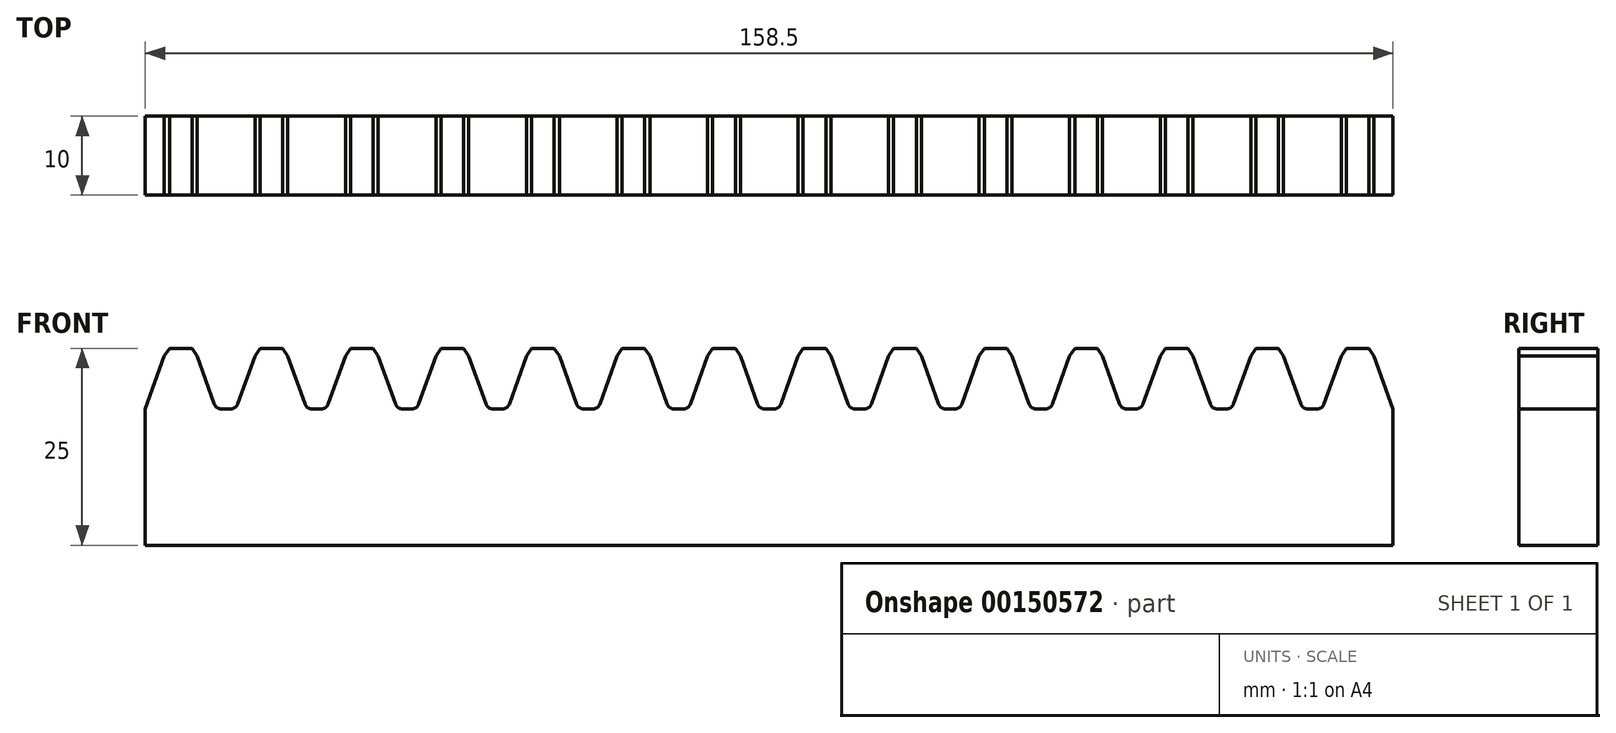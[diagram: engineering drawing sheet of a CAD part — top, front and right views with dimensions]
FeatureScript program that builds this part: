
annotation { "Feature Type Name" : "Feature", "Feature Type Description" : "" }
export const myFeature = defineFeature(function(context is Context, id is Id, definition is map)
    precondition{}
    {
        {
            var Q0;
            Q0=qCreatedBy(makeId("Front.planeOp"),FACE);
            var sketch = newSketch(context, id + "F0", { "sketchPlane" : qUnion([Q0])});
            skLineSegment(sketch, "E0", {"start": v(0, 0) * mm, "end": v(151.35, 0) * mm, "construction": true});
            skLineSegment(sketch, "E1.bottom", {"start": v(0, 0) * mm, "end": v(9, 0) * mm});
            skLineSegment(sketch, "E1.top", {"start": v(2.75, 25) * mm, "end": v(6.25, 25) * mm});
            skLineSegment(sketch, "E1.left", {"start": v(0, 0) * mm, "end": v(0, 17.3) * mm});
            skLineSegment(sketch, "E1.right", {"start": v(9, 0) * mm, "end": v(9, 17.3) * mm});
            skLineSegment(sketch, "E2", {"start": v(4.5, 0) * mm, "end": v(4.5, 25) * mm, "construction": true});
            skPoint(sketch, "E3", {"position": v(0, 17.3) * mm});
            skPoint(sketch, "E4", {"position": v(2.75, 25) * mm});
            skLineSegment(sketch, "E5", {"start": v(0, 17.3) * mm, "end": v(2.75, 25) * mm});
            skLineSegment(sketch, "E6.MirrorCS", {"start": v(9, 17.3) * mm, "end": v(6.25, 25) * mm});
            skLineSegment(sketch, "E7", {"start": v(9, 17.3) * mm, "end": v(11.5, 17.3) * mm});
            skPoint(sketch, "E8.orphan", {"position": v(0, 25) * mm});
            skPoint(sketch, "E9.orphan", {"position": v(9, 25) * mm});
            skLineSegment(sketch, "E10", {"start": v(9, 0) * mm, "end": v(11.5, 0) * mm});
            skLineSegment(sketch, "E11", {"start": v(11.5, 0) * mm, "end": v(11.5, 17.3) * mm});
            skLineSegment(sketch, "E12.1.0.1", {"start": v(11.5, 17.3) * mm, "end": v(14.25, 25) * mm});
            skLineSegment(sketch, "E12.1.0.2", {"start": v(14.25, 25) * mm, "end": v(17.75, 25) * mm});
            skLineSegment(sketch, "E12.1.0.3", {"start": v(20.5, 17.3) * mm, "end": v(17.75, 25) * mm});
            skLineSegment(sketch, "E12.1.0.4", {"start": v(20.5, 17.3) * mm, "end": v(23, 17.3) * mm});
            skLineSegment(sketch, "E12.1.0.5", {"start": v(11.5, 0) * mm, "end": v(20.5, 0) * mm});
            skLineSegment(sketch, "E12.1.0.6", {"start": v(20.5, 0) * mm, "end": v(23, 0) * mm});
            skLineSegment(sketch, "E12.2.0.0", {"start": v(23, 0) * mm, "end": v(23, 17.3) * mm});
            skLineSegment(sketch, "E12.2.0.1", {"start": v(23, 17.3) * mm, "end": v(25.75, 25) * mm});
            skLineSegment(sketch, "E12.2.0.2", {"start": v(25.75, 25) * mm, "end": v(29.25, 25) * mm});
            skLineSegment(sketch, "E12.2.0.3", {"start": v(32, 17.3) * mm, "end": v(29.25, 25) * mm});
            skLineSegment(sketch, "E12.2.0.4", {"start": v(32, 17.3) * mm, "end": v(34.5, 17.3) * mm});
            skLineSegment(sketch, "E12.2.0.5", {"start": v(23, 0) * mm, "end": v(32, 0) * mm});
            skLineSegment(sketch, "E12.2.0.6", {"start": v(32, 0) * mm, "end": v(34.5, 0) * mm});
            skLineSegment(sketch, "E12.3.0.0", {"start": v(34.5, 0) * mm, "end": v(34.5, 17.3) * mm});
            skLineSegment(sketch, "E12.3.0.1", {"start": v(34.5, 17.3) * mm, "end": v(37.25, 25) * mm});
            skLineSegment(sketch, "E12.3.0.2", {"start": v(37.25, 25) * mm, "end": v(40.75, 25) * mm});
            skLineSegment(sketch, "E12.3.0.3", {"start": v(43.5, 17.3) * mm, "end": v(40.75, 25) * mm});
            skLineSegment(sketch, "E12.3.0.4", {"start": v(43.5, 17.3) * mm, "end": v(46, 17.3) * mm});
            skLineSegment(sketch, "E12.3.0.5", {"start": v(34.5, 0) * mm, "end": v(43.5, 0) * mm});
            skLineSegment(sketch, "E12.3.0.6", {"start": v(43.5, 0) * mm, "end": v(46, 0) * mm});
            skLineSegment(sketch, "E12.4.0.0", {"start": v(46, 0) * mm, "end": v(46, 17.3) * mm});
            skLineSegment(sketch, "E12.4.0.1", {"start": v(46, 17.3) * mm, "end": v(48.75, 25) * mm});
            skLineSegment(sketch, "E12.4.0.2", {"start": v(48.75, 25) * mm, "end": v(52.25, 25) * mm});
            skLineSegment(sketch, "E12.4.0.3", {"start": v(55, 17.3) * mm, "end": v(52.25, 25) * mm});
            skLineSegment(sketch, "E12.4.0.4", {"start": v(55, 17.3) * mm, "end": v(57.5, 17.3) * mm});
            skLineSegment(sketch, "E12.4.0.5", {"start": v(46, 0) * mm, "end": v(55, 0) * mm});
            skLineSegment(sketch, "E12.4.0.6", {"start": v(55, 0) * mm, "end": v(57.5, 0) * mm});
            skLineSegment(sketch, "E12.5.0.0", {"start": v(57.5, 0) * mm, "end": v(57.5, 17.3) * mm});
            skLineSegment(sketch, "E12.5.0.1", {"start": v(57.5, 17.3) * mm, "end": v(60.25, 25) * mm});
            skLineSegment(sketch, "E12.5.0.2", {"start": v(60.25, 25) * mm, "end": v(63.75, 25) * mm});
            skLineSegment(sketch, "E12.5.0.3", {"start": v(66.5, 17.3) * mm, "end": v(63.75, 25) * mm});
            skLineSegment(sketch, "E12.5.0.4", {"start": v(66.5, 17.3) * mm, "end": v(69, 17.3) * mm});
            skLineSegment(sketch, "E12.5.0.5", {"start": v(57.5, 0) * mm, "end": v(66.5, 0) * mm});
            skLineSegment(sketch, "E12.5.0.6", {"start": v(66.5, 0) * mm, "end": v(69, 0) * mm});
            skLineSegment(sketch, "E12.6.0.0", {"start": v(69, 0) * mm, "end": v(69, 17.3) * mm});
            skLineSegment(sketch, "E12.6.0.1", {"start": v(69, 17.3) * mm, "end": v(71.75, 25) * mm});
            skLineSegment(sketch, "E12.6.0.2", {"start": v(71.75, 25) * mm, "end": v(75.25, 25) * mm});
            skLineSegment(sketch, "E12.6.0.3", {"start": v(78, 17.3) * mm, "end": v(75.25, 25) * mm});
            skLineSegment(sketch, "E12.6.0.4", {"start": v(78, 17.3) * mm, "end": v(80.5, 17.3) * mm});
            skLineSegment(sketch, "E12.6.0.5", {"start": v(69, 0) * mm, "end": v(78, 0) * mm});
            skLineSegment(sketch, "E12.6.0.6", {"start": v(78, 0) * mm, "end": v(80.5, 0) * mm});
            skLineSegment(sketch, "E12.7.0.0", {"start": v(80.5, 0) * mm, "end": v(80.5, 17.3) * mm});
            skLineSegment(sketch, "E12.7.0.1", {"start": v(80.5, 17.3) * mm, "end": v(83.25, 25) * mm});
            skLineSegment(sketch, "E12.7.0.2", {"start": v(83.25, 25) * mm, "end": v(86.75, 25) * mm});
            skLineSegment(sketch, "E12.7.0.3", {"start": v(89.5, 17.3) * mm, "end": v(86.75, 25) * mm});
            skLineSegment(sketch, "E12.7.0.4", {"start": v(89.5, 17.3) * mm, "end": v(92, 17.3) * mm});
            skLineSegment(sketch, "E12.7.0.5", {"start": v(80.5, 0) * mm, "end": v(89.5, 0) * mm});
            skLineSegment(sketch, "E12.7.0.6", {"start": v(89.5, 0) * mm, "end": v(92, 0) * mm});
            skLineSegment(sketch, "E12.8.0.0", {"start": v(92, 0) * mm, "end": v(92, 17.3) * mm});
            skLineSegment(sketch, "E12.8.0.1", {"start": v(92, 17.3) * mm, "end": v(94.75, 25) * mm});
            skLineSegment(sketch, "E12.8.0.2", {"start": v(94.75, 25) * mm, "end": v(98.25, 25) * mm});
            skLineSegment(sketch, "E12.8.0.3", {"start": v(101, 17.3) * mm, "end": v(98.25, 25) * mm});
            skLineSegment(sketch, "E12.8.0.4", {"start": v(101, 17.3) * mm, "end": v(103.5, 17.3) * mm});
            skLineSegment(sketch, "E12.8.0.5", {"start": v(92, 0) * mm, "end": v(101, 0) * mm});
            skLineSegment(sketch, "E12.8.0.6", {"start": v(101, 0) * mm, "end": v(103.5, 0) * mm});
            skLineSegment(sketch, "E12.9.0.0", {"start": v(103.5, 0) * mm, "end": v(103.5, 17.3) * mm});
            skLineSegment(sketch, "E12.9.0.1", {"start": v(103.5, 17.3) * mm, "end": v(106.25, 25) * mm});
            skLineSegment(sketch, "E12.9.0.2", {"start": v(106.25, 25) * mm, "end": v(109.75, 25) * mm});
            skLineSegment(sketch, "E12.9.0.3", {"start": v(112.5, 17.3) * mm, "end": v(109.75, 25) * mm});
            skLineSegment(sketch, "E12.9.0.4", {"start": v(112.5, 17.3) * mm, "end": v(115, 17.3) * mm});
            skLineSegment(sketch, "E12.9.0.5", {"start": v(103.5, 0) * mm, "end": v(112.5, 0) * mm});
            skLineSegment(sketch, "E12.9.0.6", {"start": v(112.5, 0) * mm, "end": v(115, 0) * mm});
            skLineSegment(sketch, "E12.10.0.0", {"start": v(115, 0) * mm, "end": v(115, 17.3) * mm});
            skLineSegment(sketch, "E12.10.0.1", {"start": v(115, 17.3) * mm, "end": v(117.75, 25) * mm});
            skLineSegment(sketch, "E12.10.0.2", {"start": v(117.75, 25) * mm, "end": v(121.25, 25) * mm});
            skLineSegment(sketch, "E12.10.0.3", {"start": v(124, 17.3) * mm, "end": v(121.25, 25) * mm});
            skLineSegment(sketch, "E12.10.0.4", {"start": v(124, 17.3) * mm, "end": v(126.5, 17.3) * mm});
            skLineSegment(sketch, "E12.10.0.5", {"start": v(115, 0) * mm, "end": v(124, 0) * mm});
            skLineSegment(sketch, "E12.10.0.6", {"start": v(124, 0) * mm, "end": v(126.5, 0) * mm});
            skLineSegment(sketch, "E12.11.0.0", {"start": v(126.5, 0) * mm, "end": v(126.5, 17.3) * mm});
            skLineSegment(sketch, "E12.11.0.1", {"start": v(126.5, 17.3) * mm, "end": v(129.25, 25) * mm});
            skLineSegment(sketch, "E12.11.0.2", {"start": v(129.25, 25) * mm, "end": v(132.75, 25) * mm});
            skLineSegment(sketch, "E12.11.0.3", {"start": v(135.5, 17.3) * mm, "end": v(132.75, 25) * mm});
            skLineSegment(sketch, "E12.11.0.4", {"start": v(135.5, 17.3) * mm, "end": v(138, 17.3) * mm});
            skLineSegment(sketch, "E12.11.0.5", {"start": v(126.5, 0) * mm, "end": v(135.5, 0) * mm});
            skLineSegment(sketch, "E12.11.0.6", {"start": v(135.5, 0) * mm, "end": v(138, 0) * mm});
            skLineSegment(sketch, "E12.12.0.0", {"start": v(138, 0) * mm, "end": v(138, 17.3) * mm});
            skLineSegment(sketch, "E12.12.0.1", {"start": v(138, 17.3) * mm, "end": v(140.75, 25) * mm});
            skLineSegment(sketch, "E12.12.0.2", {"start": v(140.75, 25) * mm, "end": v(144.25, 25) * mm});
            skLineSegment(sketch, "E12.12.0.3", {"start": v(147, 17.3) * mm, "end": v(144.25, 25) * mm});
            skLineSegment(sketch, "E12.12.0.4", {"start": v(147, 17.3) * mm, "end": v(149.5, 17.3) * mm});
            skLineSegment(sketch, "E12.12.0.5", {"start": v(138, 0) * mm, "end": v(147, 0) * mm});
            skLineSegment(sketch, "E12.12.0.6", {"start": v(147, 0) * mm, "end": v(149.5, 0) * mm});
            skLineSegment(sketch, "E12.13.0.0", {"start": v(149.5, 0) * mm, "end": v(149.5, 17.3) * mm});
            skLineSegment(sketch, "E12.13.0.1", {"start": v(149.5, 17.3) * mm, "end": v(152.25, 25) * mm});
            skLineSegment(sketch, "E12.13.0.2", {"start": v(152.25, 25) * mm, "end": v(155.75, 25) * mm});
            skLineSegment(sketch, "E12.13.0.3", {"start": v(158.5, 17.3) * mm, "end": v(155.75, 25) * mm});
            skLineSegment(sketch, "E12.13.0.5", {"start": v(149.5, 0) * mm, "end": v(158.5, 0) * mm});
            skLineSegment(sketch, "E12.direction1", {"start": v(0, 0) * mm, "end": v(11.5, 0) * mm, "construction": true});
            skLineSegment(sketch, "E13", {"start": v(158.5, 0) * mm, "end": v(158.5, 17.3) * mm});
            skSolve(sketch);
        }
        {
            var Q0;
            Q0 = qSketchRegion(id + "F0", true);
            extrude(context, id + "F1", {"entities" : qUnion([Q0]), "depth" : 10 * mm});
        }
        {
            var Q0;
            Q0=makeQuery(id+"F1.opExtrude","SWEPT_EDGE",EDGE,{"disambiguationData":[OSD([sQuery(id+"F0.wireOp",EDGE,"E1.top"),sQuery(id+"F0.wireOp",EDGE,"E5")])]});
            var Q1;
            Q1=makeQuery(id+"F1.opExtrude","SWEPT_EDGE",EDGE,{"disambiguationData":[OSD([sQuery(id+"F0.wireOp",EDGE,"E1.top"),sQuery(id+"F0.wireOp",EDGE,"E6.MirrorCS")])]});
            var Q2;
            Q2=makeQuery(id+"F1.opExtrude","SWEPT_EDGE",EDGE,{"disambiguationData":[OSD([sQuery(id+"F0.wireOp",EDGE,"E12.1.0.1"),sQuery(id+"F0.wireOp",EDGE,"E12.1.0.2")])]});
            var Q3;
            Q3=makeQuery(id+"F1.opExtrude","SWEPT_EDGE",EDGE,{"disambiguationData":[OSD([sQuery(id+"F0.wireOp",EDGE,"E12.2.0.1"),sQuery(id+"F0.wireOp",EDGE,"E12.2.0.2")])]});
            var Q4;
            Q4=makeQuery(id+"F1.opExtrude","SWEPT_EDGE",EDGE,{"disambiguationData":[OSD([sQuery(id+"F0.wireOp",EDGE,"E12.3.0.1"),sQuery(id+"F0.wireOp",EDGE,"E12.3.0.2")])]});
            var Q5;
            Q5=makeQuery(id+"F1.opExtrude","SWEPT_EDGE",EDGE,{"disambiguationData":[OSD([sQuery(id+"F0.wireOp",EDGE,"E12.4.0.1"),sQuery(id+"F0.wireOp",EDGE,"E12.4.0.2")])]});
            var Q6;
            Q6=makeQuery(id+"F1.opExtrude","SWEPT_EDGE",EDGE,{"disambiguationData":[OSD([sQuery(id+"F0.wireOp",EDGE,"E12.5.0.1"),sQuery(id+"F0.wireOp",EDGE,"E12.5.0.2")])]});
            var Q7;
            Q7=makeQuery(id+"F1.opExtrude","SWEPT_EDGE",EDGE,{"disambiguationData":[OSD([sQuery(id+"F0.wireOp",EDGE,"E12.6.0.1"),sQuery(id+"F0.wireOp",EDGE,"E12.6.0.2")])]});
            var Q8;
            Q8=makeQuery(id+"F1.opExtrude","SWEPT_EDGE",EDGE,{"disambiguationData":[OSD([sQuery(id+"F0.wireOp",EDGE,"E12.7.0.1"),sQuery(id+"F0.wireOp",EDGE,"E12.7.0.2")])]});
            var Q9;
            Q9=makeQuery(id+"F1.opExtrude","SWEPT_EDGE",EDGE,{"disambiguationData":[OSD([sQuery(id+"F0.wireOp",EDGE,"E12.8.0.1"),sQuery(id+"F0.wireOp",EDGE,"E12.8.0.2")])]});
            var Q10;
            Q10=makeQuery(id+"F1.opExtrude","SWEPT_EDGE",EDGE,{"disambiguationData":[OSD([sQuery(id+"F0.wireOp",EDGE,"E12.9.0.1"),sQuery(id+"F0.wireOp",EDGE,"E12.9.0.2")])]});
            var Q11;
            Q11=makeQuery(id+"F1.opExtrude","SWEPT_EDGE",EDGE,{"disambiguationData":[OSD([sQuery(id+"F0.wireOp",EDGE,"E12.10.0.1"),sQuery(id+"F0.wireOp",EDGE,"E12.10.0.2")])]});
            var Q12;
            Q12=makeQuery(id+"F1.opExtrude","SWEPT_EDGE",EDGE,{"disambiguationData":[OSD([sQuery(id+"F0.wireOp",EDGE,"E12.11.0.1"),sQuery(id+"F0.wireOp",EDGE,"E12.11.0.2")])]});
            var Q13;
            Q13=makeQuery(id+"F1.opExtrude","SWEPT_EDGE",EDGE,{"disambiguationData":[OSD([sQuery(id+"F0.wireOp",EDGE,"E12.12.0.1"),sQuery(id+"F0.wireOp",EDGE,"E12.12.0.2")])]});
            var Q14;
            Q14=makeQuery(id+"F1.opExtrude","SWEPT_EDGE",EDGE,{"disambiguationData":[OSD([sQuery(id+"F0.wireOp",EDGE,"E12.13.0.1"),sQuery(id+"F0.wireOp",EDGE,"E12.13.0.2")])]});
            chamfer(context, id + "F2", {"entities" : qUnion([Q0, Q1, Q2, Q3, Q4, Q5, Q6, Q7, Q8, Q9, Q10, Q11, Q12, Q13, Q14]), "chamferType" : ChamferType.OFFSET_ANGLE, "width" : 1 * mm, "oppositeDirection" : false, "angle" : 15 * degree, "tangentPropagation" : true});
        }
        {
            var Q0;
            Q0=makeQuery(id+"F1.opExtrude","SWEPT_EDGE",EDGE,{"disambiguationData":[OSD([sQuery(id+"F0.wireOp",EDGE,"E12.13.0.2"),sQuery(id+"F0.wireOp",EDGE,"E12.13.0.3")])]});
            var Q1;
            Q1=makeQuery(id+"F1.opExtrude","SWEPT_EDGE",EDGE,{"disambiguationData":[OSD([sQuery(id+"F0.wireOp",EDGE,"E12.12.0.2"),sQuery(id+"F0.wireOp",EDGE,"E12.12.0.3")])]});
            var Q2;
            Q2=makeQuery(id+"F1.opExtrude","SWEPT_EDGE",EDGE,{"disambiguationData":[OSD([sQuery(id+"F0.wireOp",EDGE,"E12.11.0.2"),sQuery(id+"F0.wireOp",EDGE,"E12.11.0.3")])]});
            var Q3;
            Q3=makeQuery(id+"F1.opExtrude","SWEPT_EDGE",EDGE,{"disambiguationData":[OSD([sQuery(id+"F0.wireOp",EDGE,"E12.10.0.2"),sQuery(id+"F0.wireOp",EDGE,"E12.10.0.3")])]});
            var Q4;
            Q4=makeQuery(id+"F1.opExtrude","SWEPT_EDGE",EDGE,{"disambiguationData":[OSD([sQuery(id+"F0.wireOp",EDGE,"E12.9.0.2"),sQuery(id+"F0.wireOp",EDGE,"E12.9.0.3")])]});
            var Q5;
            Q5=makeQuery(id+"F1.opExtrude","SWEPT_EDGE",EDGE,{"disambiguationData":[OSD([sQuery(id+"F0.wireOp",EDGE,"E12.8.0.2"),sQuery(id+"F0.wireOp",EDGE,"E12.8.0.3")])]});
            var Q6;
            Q6=makeQuery(id+"F1.opExtrude","SWEPT_EDGE",EDGE,{"disambiguationData":[OSD([sQuery(id+"F0.wireOp",EDGE,"E12.7.0.2"),sQuery(id+"F0.wireOp",EDGE,"E12.7.0.3")])]});
            var Q7;
            Q7=makeQuery(id+"F1.opExtrude","SWEPT_EDGE",EDGE,{"disambiguationData":[OSD([sQuery(id+"F0.wireOp",EDGE,"E12.6.0.2"),sQuery(id+"F0.wireOp",EDGE,"E12.6.0.3")])]});
            var Q8;
            Q8=makeQuery(id+"F1.opExtrude","SWEPT_EDGE",EDGE,{"disambiguationData":[OSD([sQuery(id+"F0.wireOp",EDGE,"E12.5.0.2"),sQuery(id+"F0.wireOp",EDGE,"E12.5.0.3")])]});
            var Q9;
            Q9=makeQuery(id+"F1.opExtrude","SWEPT_EDGE",EDGE,{"disambiguationData":[OSD([sQuery(id+"F0.wireOp",EDGE,"E12.4.0.2"),sQuery(id+"F0.wireOp",EDGE,"E12.4.0.3")])]});
            var Q10;
            Q10=makeQuery(id+"F1.opExtrude","SWEPT_EDGE",EDGE,{"disambiguationData":[OSD([sQuery(id+"F0.wireOp",EDGE,"E12.3.0.2"),sQuery(id+"F0.wireOp",EDGE,"E12.3.0.3")])]});
            var Q11;
            Q11=makeQuery(id+"F1.opExtrude","SWEPT_EDGE",EDGE,{"disambiguationData":[OSD([sQuery(id+"F0.wireOp",EDGE,"E12.2.0.2"),sQuery(id+"F0.wireOp",EDGE,"E12.2.0.3")])]});
            var Q12;
            Q12=makeQuery(id+"F1.opExtrude","SWEPT_EDGE",EDGE,{"disambiguationData":[OSD([sQuery(id+"F0.wireOp",EDGE,"E12.1.0.2"),sQuery(id+"F0.wireOp",EDGE,"E12.1.0.3")])]});
            chamfer(context, id + "F3", {"entities" : qUnion([Q0, Q1, Q2, Q3, Q4, Q5, Q6, Q7, Q8, Q9, Q10, Q11, Q12]), "chamferType" : ChamferType.OFFSET_ANGLE, "width" : 1 * mm, "oppositeDirection" : true, "angle" : 15 * degree, "tangentPropagation" : true});
        }
        {
            var Q0;
            Q0=makeQuery(id+"F1.opExtrude","SWEPT_EDGE",EDGE,{"disambiguationData":[OSD([sQuery(id+"F0.wireOp",EDGE,"E1.right"),sQuery(id+"F0.wireOp",EDGE,"E6.MirrorCS"),sQuery(id+"F0.wireOp",EDGE,"E7")])]});
            var Q1;
            Q1=makeQuery(id+"F1.opExtrude","SWEPT_EDGE",EDGE,{"disambiguationData":[OSD([sQuery(id+"F0.wireOp",EDGE,"E7"),sQuery(id+"F0.wireOp",EDGE,"E11"),sQuery(id+"F0.wireOp",EDGE,"E12.1.0.1")])]});
            var Q2;
            Q2=makeQuery(id+"F1.opExtrude","SWEPT_EDGE",EDGE,{"disambiguationData":[OSD([sQuery(id+"F0.wireOp",EDGE,"E12.1.0.3"),sQuery(id+"F0.wireOp",EDGE,"E12.1.0.4")])]});
            var Q3;
            Q3=makeQuery(id+"F1.opExtrude","SWEPT_EDGE",EDGE,{"disambiguationData":[OSD([sQuery(id+"F0.wireOp",EDGE,"E12.1.0.4"),sQuery(id+"F0.wireOp",EDGE,"E12.2.0.0"),sQuery(id+"F0.wireOp",EDGE,"E12.2.0.1")])]});
            var Q4;
            Q4=makeQuery(id+"F1.opExtrude","SWEPT_EDGE",EDGE,{"disambiguationData":[OSD([sQuery(id+"F0.wireOp",EDGE,"E12.2.0.3"),sQuery(id+"F0.wireOp",EDGE,"E12.2.0.4")])]});
            var Q5;
            Q5=makeQuery(id+"F1.opExtrude","SWEPT_EDGE",EDGE,{"disambiguationData":[OSD([sQuery(id+"F0.wireOp",EDGE,"E12.2.0.4"),sQuery(id+"F0.wireOp",EDGE,"E12.3.0.0"),sQuery(id+"F0.wireOp",EDGE,"E12.3.0.1")])]});
            var Q6;
            Q6=makeQuery(id+"F1.opExtrude","SWEPT_EDGE",EDGE,{"disambiguationData":[OSD([sQuery(id+"F0.wireOp",EDGE,"E12.3.0.3"),sQuery(id+"F0.wireOp",EDGE,"E12.3.0.4")])]});
            var Q7;
            Q7=makeQuery(id+"F1.opExtrude","SWEPT_EDGE",EDGE,{"disambiguationData":[OSD([sQuery(id+"F0.wireOp",EDGE,"E12.3.0.4"),sQuery(id+"F0.wireOp",EDGE,"E12.4.0.0"),sQuery(id+"F0.wireOp",EDGE,"E12.4.0.1")])]});
            var Q8;
            Q8=makeQuery(id+"F1.opExtrude","SWEPT_EDGE",EDGE,{"disambiguationData":[OSD([sQuery(id+"F0.wireOp",EDGE,"E12.4.0.3"),sQuery(id+"F0.wireOp",EDGE,"E12.4.0.4")])]});
            var Q9;
            Q9=makeQuery(id+"F1.opExtrude","SWEPT_EDGE",EDGE,{"disambiguationData":[OSD([sQuery(id+"F0.wireOp",EDGE,"E12.4.0.4"),sQuery(id+"F0.wireOp",EDGE,"E12.5.0.0"),sQuery(id+"F0.wireOp",EDGE,"E12.5.0.1")])]});
            var Q10;
            Q10=makeQuery(id+"F1.opExtrude","SWEPT_EDGE",EDGE,{"disambiguationData":[OSD([sQuery(id+"F0.wireOp",EDGE,"E12.5.0.3"),sQuery(id+"F0.wireOp",EDGE,"E12.5.0.4")])]});
            var Q11;
            Q11=makeQuery(id+"F1.opExtrude","SWEPT_EDGE",EDGE,{"disambiguationData":[OSD([sQuery(id+"F0.wireOp",EDGE,"E12.5.0.4"),sQuery(id+"F0.wireOp",EDGE,"E12.6.0.0"),sQuery(id+"F0.wireOp",EDGE,"E12.6.0.1")])]});
            var Q12;
            Q12=makeQuery(id+"F1.opExtrude","SWEPT_EDGE",EDGE,{"disambiguationData":[OSD([sQuery(id+"F0.wireOp",EDGE,"E12.6.0.3"),sQuery(id+"F0.wireOp",EDGE,"E12.6.0.4")])]});
            var Q13;
            Q13=makeQuery(id+"F1.opExtrude","SWEPT_EDGE",EDGE,{"disambiguationData":[OSD([sQuery(id+"F0.wireOp",EDGE,"E12.6.0.4"),sQuery(id+"F0.wireOp",EDGE,"E12.7.0.0"),sQuery(id+"F0.wireOp",EDGE,"E12.7.0.1")])]});
            var Q14;
            Q14=makeQuery(id+"F1.opExtrude","SWEPT_EDGE",EDGE,{"disambiguationData":[OSD([sQuery(id+"F0.wireOp",EDGE,"E12.7.0.3"),sQuery(id+"F0.wireOp",EDGE,"E12.7.0.4")])]});
            var Q15;
            Q15=makeQuery(id+"F1.opExtrude","SWEPT_EDGE",EDGE,{"disambiguationData":[OSD([sQuery(id+"F0.wireOp",EDGE,"E12.8.0.3"),sQuery(id+"F0.wireOp",EDGE,"E12.8.0.4")])]});
            var Q16;
            Q16=makeQuery(id+"F1.opExtrude","SWEPT_EDGE",EDGE,{"disambiguationData":[OSD([sQuery(id+"F0.wireOp",EDGE,"E12.7.0.4"),sQuery(id+"F0.wireOp",EDGE,"E12.8.0.0"),sQuery(id+"F0.wireOp",EDGE,"E12.8.0.1")])]});
            var Q17;
            Q17=makeQuery(id+"F1.opExtrude","SWEPT_EDGE",EDGE,{"disambiguationData":[OSD([sQuery(id+"F0.wireOp",EDGE,"E12.8.0.4"),sQuery(id+"F0.wireOp",EDGE,"E12.9.0.0"),sQuery(id+"F0.wireOp",EDGE,"E12.9.0.1")])]});
            var Q18;
            Q18=makeQuery(id+"F1.opExtrude","SWEPT_EDGE",EDGE,{"disambiguationData":[OSD([sQuery(id+"F0.wireOp",EDGE,"E12.9.0.3"),sQuery(id+"F0.wireOp",EDGE,"E12.9.0.4")])]});
            var Q19;
            Q19=makeQuery(id+"F1.opExtrude","SWEPT_EDGE",EDGE,{"disambiguationData":[OSD([sQuery(id+"F0.wireOp",EDGE,"E12.9.0.4"),sQuery(id+"F0.wireOp",EDGE,"E12.10.0.0"),sQuery(id+"F0.wireOp",EDGE,"E12.10.0.1")])]});
            var Q20;
            Q20=makeQuery(id+"F1.opExtrude","SWEPT_EDGE",EDGE,{"disambiguationData":[OSD([sQuery(id+"F0.wireOp",EDGE,"E12.10.0.3"),sQuery(id+"F0.wireOp",EDGE,"E12.10.0.4")])]});
            var Q21;
            Q21=makeQuery(id+"F1.opExtrude","SWEPT_EDGE",EDGE,{"disambiguationData":[OSD([sQuery(id+"F0.wireOp",EDGE,"E12.10.0.4"),sQuery(id+"F0.wireOp",EDGE,"E12.11.0.0"),sQuery(id+"F0.wireOp",EDGE,"E12.11.0.1")])]});
            var Q22;
            Q22=makeQuery(id+"F1.opExtrude","SWEPT_EDGE",EDGE,{"disambiguationData":[OSD([sQuery(id+"F0.wireOp",EDGE,"E12.11.0.3"),sQuery(id+"F0.wireOp",EDGE,"E12.11.0.4")])]});
            var Q23;
            Q23=makeQuery(id+"F1.opExtrude","SWEPT_EDGE",EDGE,{"disambiguationData":[OSD([sQuery(id+"F0.wireOp",EDGE,"E12.11.0.4"),sQuery(id+"F0.wireOp",EDGE,"E12.12.0.0"),sQuery(id+"F0.wireOp",EDGE,"E12.12.0.1")])]});
            var Q24;
            Q24=makeQuery(id+"F1.opExtrude","SWEPT_EDGE",EDGE,{"disambiguationData":[OSD([sQuery(id+"F0.wireOp",EDGE,"E12.12.0.3"),sQuery(id+"F0.wireOp",EDGE,"E12.12.0.4")])]});
            var Q25;
            Q25=makeQuery(id+"F1.opExtrude","SWEPT_EDGE",EDGE,{"disambiguationData":[OSD([sQuery(id+"F0.wireOp",EDGE,"E12.12.0.4"),sQuery(id+"F0.wireOp",EDGE,"E12.13.0.0"),sQuery(id+"F0.wireOp",EDGE,"E12.13.0.1")])]});
            fillet(context, id + "F4", {"entities" : qUnion([Q0, Q1, Q2, Q3, Q4, Q5, Q6, Q7, Q8, Q9, Q10, Q11, Q12, Q13, Q14, Q15, Q16, Q17, Q18, Q19, Q20, Q21, Q22, Q23, Q24, Q25]), "radius" : 1 * mm, "tangentPropagation" : true, "allowEdgeOverflow" : false});
        }
    });
